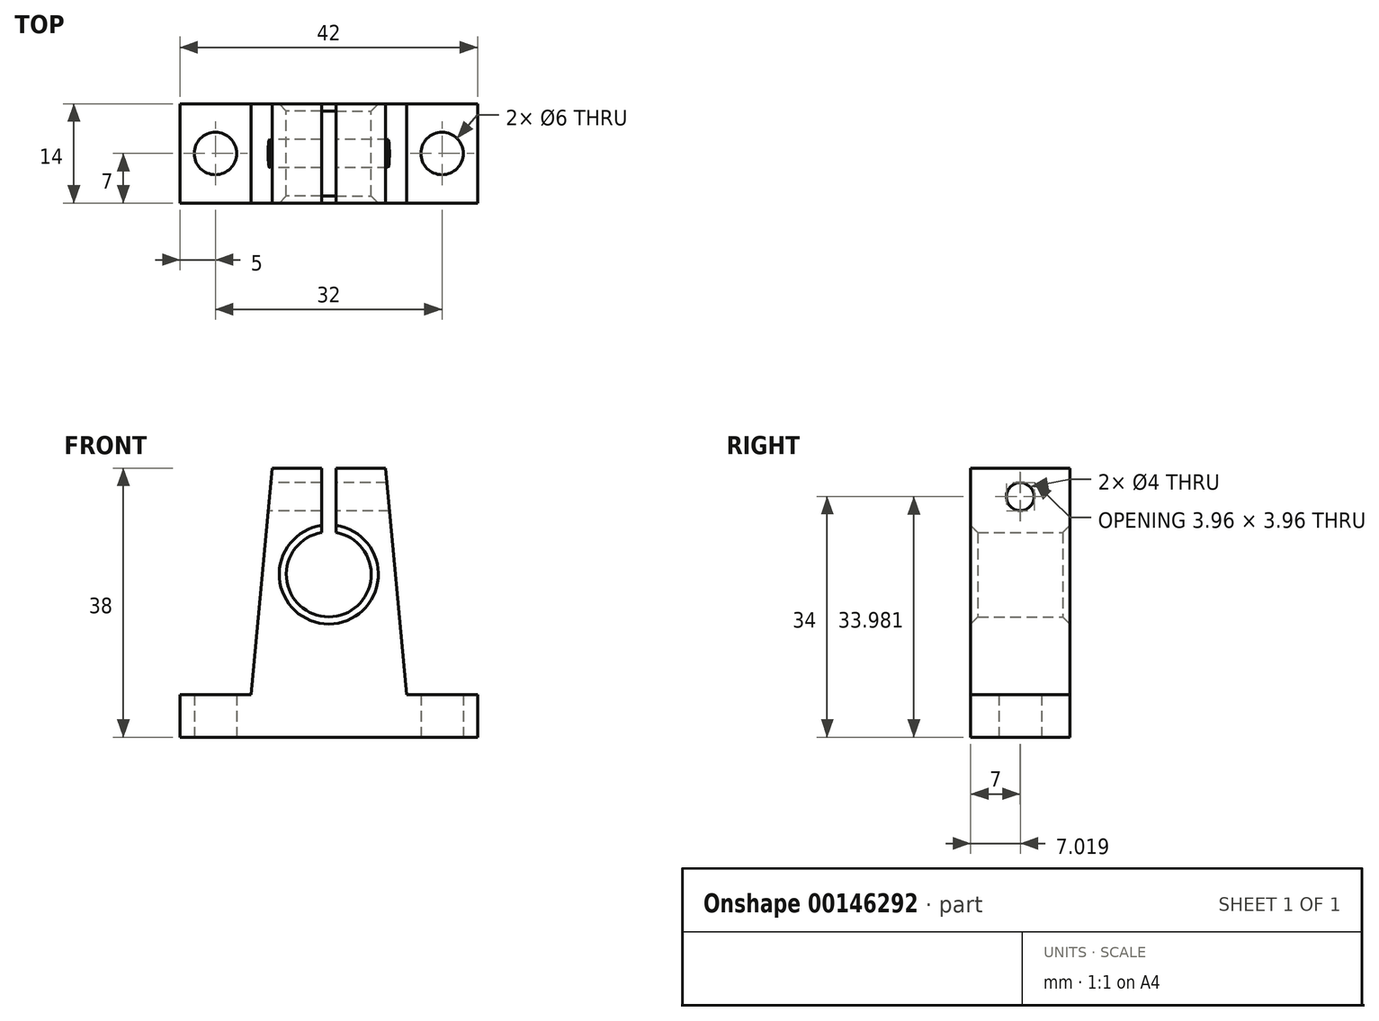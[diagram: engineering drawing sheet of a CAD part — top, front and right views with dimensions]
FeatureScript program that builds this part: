
annotation { "Feature Type Name" : "Feature", "Feature Type Description" : "" }
export const myFeature = defineFeature(function(context is Context, id is Id, definition is map)
    precondition{}
    {
        {
            var Q0;
            Q0=qCreatedBy(makeId("Top.planeOp"),FACE);
            var sketch = newSketch(context, id + "F0", { "sketchPlane" : qUnion([Q0])});
            skLineSegment(sketch, "E0", {"start": v(-21, 0) * mm, "end": v(21, 0) * mm});
            skLineSegment(sketch, "E1", {"start": v(21, 0) * mm, "end": v(21, 6) * mm});
            skLineSegment(sketch, "E2", {"start": v(21, 6) * mm, "end": v(11, 6) * mm});
            skLineSegment(sketch, "E3", {"start": v(11, 6) * mm, "end": v(8, 38) * mm});
            skLineSegment(sketch, "E4", {"start": v(8, 38) * mm, "end": v(-8, 38) * mm});
            skLineSegment(sketch, "E5", {"start": v(-8, 38) * mm, "end": v(-11, 6) * mm});
            skLineSegment(sketch, "E6", {"start": v(-11, 6) * mm, "end": v(-21, 6) * mm});
            skLineSegment(sketch, "E7", {"start": v(-21, 6) * mm, "end": v(-21, 0) * mm});
            skCircle(sketch, "E8", {"center": v(0, 23) * mm, "radius": 6 * mm});
            skLineSegment(sketch, "E9", {"start": v(0, 38) * mm, "end": v(-1, 38) * mm});
            skLineSegment(sketch, "E10.bottom", {"start": v(-1, 38) * mm, "end": v(1, 38) * mm});
            skLineSegment(sketch, "E10.top", {"start": v(-1, 28.92) * mm, "end": v(1, 28.92) * mm});
            skLineSegment(sketch, "E10.left", {"start": v(-1, 38) * mm, "end": v(-1, 28.92) * mm});
            skLineSegment(sketch, "E10.right", {"start": v(1, 38) * mm, "end": v(1, 28.92) * mm});
            skPoint(sketch, "E11.visualSharp", {"position": v(-11, 6) * mm});
            skPoint(sketch, "E12.visualSharp", {"position": v(11, 6) * mm});
            skPoint(sketch, "E13.visualSharp", {"position": v(-8, 38) * mm});
            skPoint(sketch, "E14.visualSharp", {"position": v(8, 38) * mm});
            skPoint(sketch, "E15.visualSharp", {"position": v(-21, 6) * mm});
            skPoint(sketch, "E16.visualSharp", {"position": v(21, 6) * mm});
            skPoint(sketch, "E17", {"position": v(0, 0) * mm});
            skSolve(sketch);
        }
        {
            var Q0;
            Q0=makeQuery(id+"F0.imprint","IMPRINT",FACE,{"disambiguationData":[TD([[makeQuery(id+"F0.imprint","IMPRINT",EDGE,{"derivedFrom":sQuery(id+"F0.wireOp",EDGE,"E0")}),1.0]])]});
            extrude(context, id + "F1", {"entities" : qUnion([Q0]), "depth" : 14 * mm});
        }
        {
            var Q0;
            Q0=makeQuery(id+"F1.opExtrude","SWEPT_FACE",FACE,{"disambiguationData":[OSD([sQuery(id+"F0.wireOp",EDGE,"E0")])]});
            var sketch = newSketch(context, id + "F2", { "sketchPlane" : qUnion([Q0])});
            skPoint(sketch, "E18", {"position": v(0, 7) * mm});
            skCircle(sketch, "E19", {"center": v(-16, 7) * mm, "radius": 3 * mm});
            skCircle(sketch, "E20", {"center": v(16, 7) * mm, "radius": 3 * mm});
            skLineSegment(sketch, "E21", {"start": v(0, 14) * mm, "end": v(0, 0) * mm, "construction": true});
            skLineSegment(sketch, "E22", {"start": v(-16, 7) * mm, "end": v(0, 7) * mm, "construction": true});
            skLineSegment(sketch, "E23", {"start": v(0, 7) * mm, "end": v(16, 7) * mm, "construction": true});
            skSolve(sketch);
        }
        {
            var Q0;
            Q0 = qSketchRegion(id + "F2", true);
            extrude(context, id + "F3", {"entities" : qUnion([Q0]), "operationType" : NewBodyOperationType.REMOVE, "endBound" : BoundingType.THROUGH_ALL, "oppositeDirection" : true, "depth" : 25 * mm});
        }
        {
            var Q0;
            Q0=makeQuery(id+"F1.opExtrude","CAP_EDGE",EDGE,{"disambiguationData":[OSD([sQuery(id+"F0.wireOp",EDGE,"E8")])],"isStart":false});
            var Q1;
            Q1=makeQuery(id+"F1.opExtrude","CAP_EDGE",EDGE,{"disambiguationData":[OSD([sQuery(id+"F0.wireOp",EDGE,"E8")])],"isStart":true});
            chamfer(context, id + "F4", {"entities" : qUnion([Q0, Q1]), "width" : 1 * mm, "tangentPropagation" : true});
        }
        {
            var Q0;
            Q0=makeQuery(id+"F1.opExtrude","SWEPT_FACE",FACE,{"disambiguationData":[OSD([sQuery(id+"F0.wireOp",EDGE,"E7")])]});
            var sketch = newSketch(context, id + "F5", { "sketchPlane" : qUnion([Q0])});
            skLineSegment(sketch, "E24.0", {"start": v(-38, 14) * mm, "end": v(-38, 0) * mm});
            skLineSegment(sketch, "E25", {"start": v(-38, 7) * mm, "end": v(-26.17, 7) * mm, "construction": true});
            skCircle(sketch, "E26", {"center": v(-34, 7) * mm, "radius": 2 * mm});
            skSolve(sketch);
        }
        {
            var Q0;
            Q0 = qSketchRegion(id + "F5", true);
            extrude(context, id + "F6", {"entities" : qUnion([Q0]), "operationType" : NewBodyOperationType.REMOVE, "endBound" : BoundingType.THROUGH_ALL, "oppositeDirection" : true, "depth" : 25 * mm});
        }
        {
            var Q0;
            Q0=makeQuery(id+"F1.opExtrude","SWEPT_BODY",BODY,{"disambiguationData":[OSD([sQuery(id+"F0.wireOp",EDGE,"E0"),sQuery(id+"F0.wireOp",EDGE,"E1"),sQuery(id+"F0.wireOp",EDGE,"E2"),sQuery(id+"F0.wireOp",EDGE,"E3"),sQuery(id+"F0.wireOp",EDGE,"E4"),sQuery(id+"F0.wireOp",EDGE,"E5"),sQuery(id+"F0.wireOp",EDGE,"E6"),sQuery(id+"F0.wireOp",EDGE,"E7"),sQuery(id+"F0.wireOp",EDGE,"E8"),sQuery(id+"F0.wireOp",EDGE,"E10.left"),sQuery(id+"F0.wireOp",EDGE,"E10.right")])]});
            var Q1;
            Q1=makeQuery(id+"F1.opExtrude","CAP_EDGE",EDGE,{"disambiguationData":[OSD([sQuery(id+"F0.wireOp",EDGE,"E0")])],"isStart":true});
            var Q2;
            Q2=makeQuery(id+"F1.opExtrude","CAP_EDGE",EDGE,{"disambiguationData":[OSD([sQuery(id+"F0.wireOp",EDGE,"E0")])],"isStart":true});
            transform(context, id + "F7", {"entities" : qUnion([Q0]), "transformType" : TransformType.ROTATION, "transformAxis" : qUnion([Q2]), "angle" : 90 * degree, "makeCopy" : false});
        }
    });
